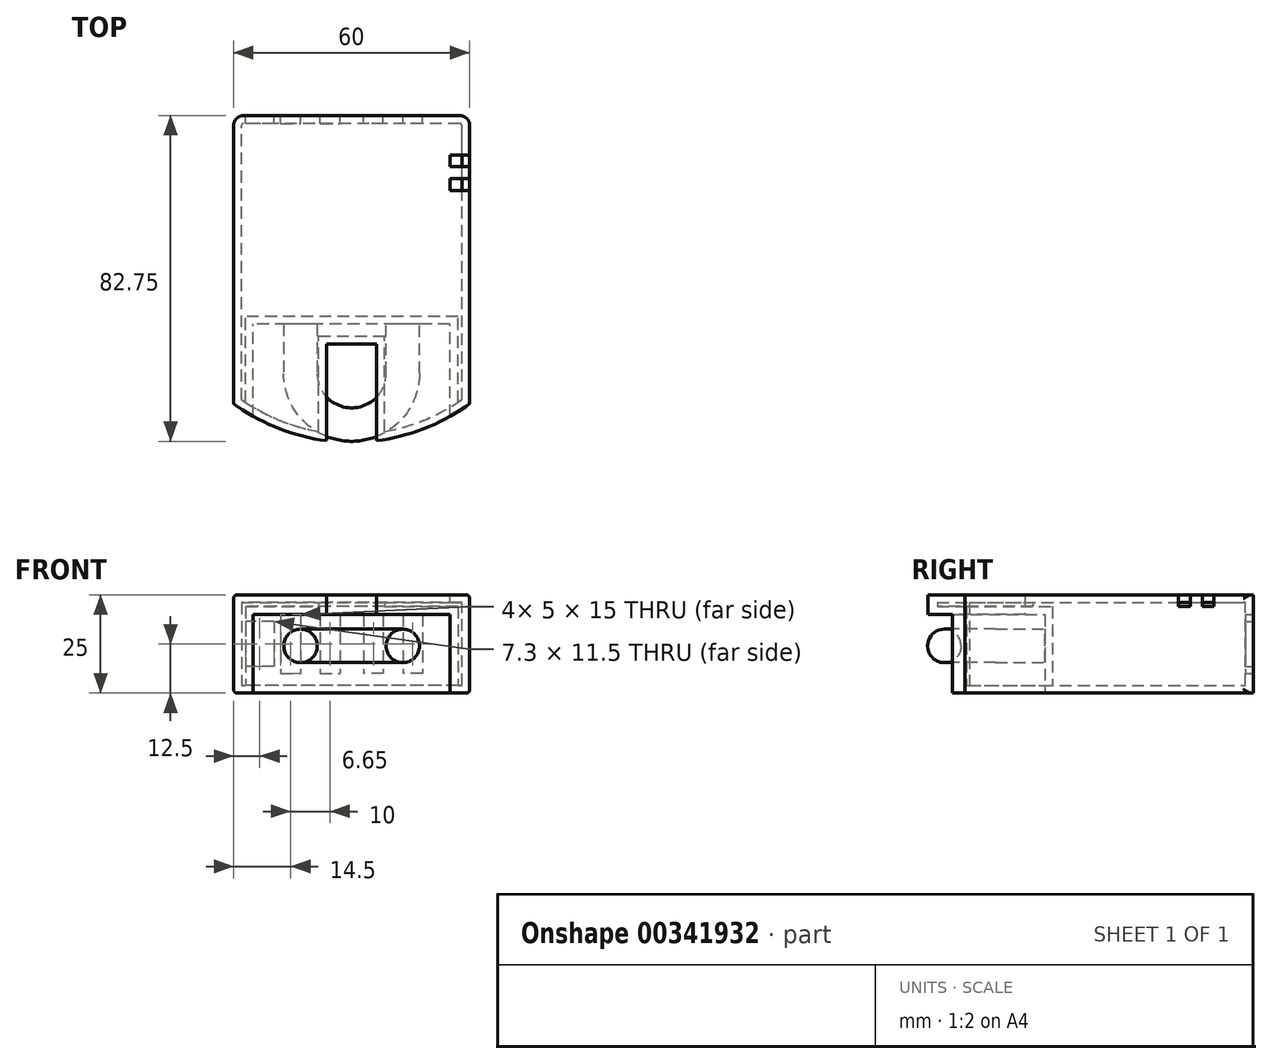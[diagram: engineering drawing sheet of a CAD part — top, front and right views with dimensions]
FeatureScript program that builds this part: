
annotation { "Feature Type Name" : "Feature", "Feature Type Description" : "" }
export const myFeature = defineFeature(function(context is Context, id is Id, definition is map)
    precondition{}
    {
        {
            var Q0;
            Q0=qCreatedBy(makeId("Top.planeOp"),FACE);
            var sketch = newSketch(context, id + "F0", { "sketchPlane" : qUnion([Q0])});
            skLineSegment(sketch, "E0.top", {"start": v(30, 36.6) * mm, "end": v(-30, 36.6) * mm});
            skLineSegment(sketch, "E0.left", {"start": v(30, -36.6) * mm, "end": v(30, 36.6) * mm});
            skLineSegment(sketch, "E0.right", {"start": v(-30, -36.6) * mm, "end": v(-30, 36.6) * mm});
            skPoint(sketch, "E0.middle", {"position": v(0, 0) * mm});
            skArc(sketch, "E1", {"start": v(-30, -36.6) * mm, "mid": v(0, -46.4) * mm, "end": v(30, -36.6) * mm});
            skSolve(sketch);
        }
        {
            var Q0;
            Q0=makeQuery(id+"F0.imprint","IMPRINT",FACE,{"disambiguationData":[TD([[makeQuery(id+"F0.imprint","IMPRINT",EDGE,{"derivedFrom":sQuery(id+"F0.wireOp",EDGE,"E0.bottom")}),-1.0]])]});
            var Q1;
            Q1=makeQuery(id+"F0.imprint","IMPRINT",FACE,{"disambiguationData":[TD([[makeQuery(id+"F0.imprint","IMPRINT",EDGE,{"derivedFrom":sQuery(id+"F0.wireOp",EDGE,"E0.top")}),1.0]])]});
            extrude(context, id + "F1", {"entities" : qUnion([Q0, Q1]), "depth" : 25 * mm});
        }
        {
            var Q0;
            Q0=qCreatedBy(makeId("Top.planeOp"),FACE);
            var sketch = newSketch(context, id + "F2", { "sketchPlane" : qUnion([Q0])});
            skLineSegment(sketch, "E2.bottom", {"start": v(-6.35, -46.4) * mm, "end": v(6.35, -46.4) * mm});
            skLineSegment(sketch, "E2.top", {"start": v(-6.35, -21.4) * mm, "end": v(6.35, -21.4) * mm});
            skLineSegment(sketch, "E2.left", {"start": v(-6.35, -46.4) * mm, "end": v(-6.35, -21.4) * mm});
            skLineSegment(sketch, "E2.right", {"start": v(6.35, -46.4) * mm, "end": v(6.35, -21.4) * mm});
            skPoint(sketch, "E2.middle", {"position": v(0, -33.9) * mm});
            skSolve(sketch);
        }
        {
            var Q0;
            Q0=makeQuery(id+"F1.opExtrude","SWEPT_EDGE",EDGE,{"disambiguationData":[OSD([sQuery(id+"F0.wireOp",EDGE,"E0.top"),sQuery(id+"F0.wireOp",EDGE,"E0.right")])]});
            var Q1;
            Q1=makeQuery(id+"F1.opExtrude","SWEPT_EDGE",EDGE,{"disambiguationData":[OSD([sQuery(id+"F0.wireOp",EDGE,"E0.top"),sQuery(id+"F0.wireOp",EDGE,"E0.left")])]});
            fillet(context, id + "F3", {"entities" : qUnion([Q0, Q1]), "radius" : 2.54 * mm, "tangentPropagation" : true, "allowEdgeOverflow" : false});
        }
        {
            var Q0;
            Q0=makeQuery(id+"F0.imprint","IMPRINT",FACE,{"disambiguationData":[TD([[makeQuery(id+"F0.imprint","IMPRINT",EDGE,{"derivedFrom":sQuery(id+"F0.wireOp",EDGE,"E0.top")}),1.0]])]});
            var sketch = newSketch(context, id + "F4", { "sketchPlane" : qUnion([Q0])});
            skLineSegment(sketch, "E3.bottom", {"start": v(25, -46.4) * mm, "end": v(-25, -46.4) * mm});
            skLineSegment(sketch, "E3.top", {"start": v(25, -16.4) * mm, "end": v(-25, -16.4) * mm});
            skLineSegment(sketch, "E3.left", {"start": v(25, -46.4) * mm, "end": v(25, -16.4) * mm});
            skLineSegment(sketch, "E3.right", {"start": v(-25, -46.4) * mm, "end": v(-25, -16.4) * mm});
            skPoint(sketch, "E3.middle", {"position": v(0, -31.4) * mm});
            skSolve(sketch);
        }
        {
            var Q0;
            Q0 = qSketchRegion(id + "F4", true);
            extrude(context, id + "F5", {"entities" : qUnion([Q0]), "operationType" : NewBodyOperationType.REMOVE, "depth" : 20 * mm});
        }
        {
            var Q0;
            Q0 = qSketchRegion(id + "F2", true);
            var Q1;
            Q1=makeQuery(id+"F1.opExtrude","CAP_FACE",FACE,{"disambiguationData":[OSD([sQuery(id+"F0.wireOp",EDGE,"E0.top"),sQuery(id+"F0.wireOp",EDGE,"E0.left"),sQuery(id+"F0.wireOp",EDGE,"E0.right"),sQuery(id+"F0.wireOp",EDGE,"E1")])],"isStart":false});
            extrude(context, id + "F6", {"entities" : qUnion([Q0]), "operationType" : NewBodyOperationType.REMOVE, "endBound" : BoundingType.UP_TO_SURFACE, "endBoundEntityFace" : qUnion([Q1]), "depth" : 25.4 * mm});
        }
        {
            var Q0;
            Q0=makeQuery(id+"F1.opExtrude","CAP_FACE",FACE,{"disambiguationData":[OSD([sQuery(id+"F0.wireOp",EDGE,"E0.top"),sQuery(id+"F0.wireOp",EDGE,"E0.left"),sQuery(id+"F0.wireOp",EDGE,"E0.right"),sQuery(id+"F0.wireOp",EDGE,"E1")])],"isStart":false});
            var Q1;
            Q1=makeQuery(id+"F1.opExtrude","SWEPT_BODY",BODY,{"disambiguationData":[OSD([sQuery(id+"F0.wireOp",EDGE,"E0.top"),sQuery(id+"F0.wireOp",EDGE,"E0.left"),sQuery(id+"F0.wireOp",EDGE,"E0.right"),sQuery(id+"F0.wireOp",EDGE,"E1")])]});
            shell(context, id + "F7", {"isHollow" : true, "entities" : qUnion([Q0]), "parts" : qUnion([Q1]), "thickness" : 2 * mm});
        }
        {
            var Q0;
            Q0=makeQuery(id+"F1.opExtrude","CAP_EDGE",EDGE,{"disambiguationData":[OSD([sQuery(id+"F0.wireOp",EDGE,"E0.left")])],"isStart":true});
            var Q1;
            Q1=makeQuery(id+"F1.opExtrude","CAP_EDGE",EDGE,{"disambiguationData":[OSD([sQuery(id+"F0.wireOp",EDGE,"E0.left")])],"isStart":false});
            var Q2;
            Q2=makeQuery(id+"F1.opExtrude","CAP_EDGE",EDGE,{"disambiguationData":[OSD([sQuery(id+"F0.wireOp",EDGE,"E0.right")])],"isStart":false});
            var Q3;
            Q3=makeQuery(id+"F1.opExtrude","CAP_EDGE",EDGE,{"disambiguationData":[OSD([sQuery(id+"F0.wireOp",EDGE,"E0.right")])],"isStart":true});
            fillet(context, id + "F8", {"entities" : qUnion([Q0, Q1, Q2, Q3]), "radius" : 1 * mm, "allowEdgeOverflow" : false});
        }
        {
            var Q0;
            Q0=makeQuery(id+"F5.boolean.opBoolean","COPY",FACE,{"derivedFrom":makeQuery(id+"F5.opExtrude","SWEPT_FACE",FACE,{"disambiguationData":[OSD([sQuery(id+"F4.wireOp",EDGE,"E3.top")])]})});
            var sketch = newSketch(context, id + "F9", { "sketchPlane" : qUnion([Q0])});
            skCircle(sketch, "E4", {"center": v(-13, 12) * mm, "radius": 5 * mm});
            skCircle(sketch, "E5.MirrorC", {"center": v(13, 12) * mm, "radius": 5 * mm});
            skSolve(sketch);
        }
        {
            var Q0;
            Q0=makeQuery(id+"F1.opExtrude","SWEPT_FACE",FACE,{"disambiguationData":[OSD([sQuery(id+"F0.wireOp",EDGE,"E0.top")])]});
            var sketch = newSketch(context, id + "F10", { "sketchPlane" : qUnion([Q0])});
            skLineSegment(sketch, "E6.bottom", {"start": v(-13, 5) * mm, "end": v(-18, 5) * mm});
            skLineSegment(sketch, "E6.top", {"start": v(-13, 20) * mm, "end": v(-18, 20) * mm});
            skLineSegment(sketch, "E6.left", {"start": v(-13, 5) * mm, "end": v(-13, 20) * mm});
            skLineSegment(sketch, "E6.right", {"start": v(-18, 5) * mm, "end": v(-18, 20) * mm});
            skPoint(sketch, "E6.middle", {"position": v(-15.5, 12.5) * mm});
            skLineSegment(sketch, "E7.MirrorCS", {"start": v(13, 5) * mm, "end": v(13, 20) * mm});
            skLineSegment(sketch, "E8.MirrorCS", {"start": v(13, 20) * mm, "end": v(18, 20) * mm});
            skLineSegment(sketch, "E9.MirrorCS", {"start": v(18, 5) * mm, "end": v(18, 20) * mm});
            skLineSegment(sketch, "E10.MirrorCS", {"start": v(13, 5) * mm, "end": v(18, 5) * mm});
            skLineSegment(sketch, "E11.bottom", {"start": v(-3, 5) * mm, "end": v(-8, 5) * mm});
            skLineSegment(sketch, "E11.top", {"start": v(-3, 20) * mm, "end": v(-8, 20) * mm});
            skLineSegment(sketch, "E11.left", {"start": v(-3, 5) * mm, "end": v(-3, 20) * mm});
            skLineSegment(sketch, "E11.right", {"start": v(-8, 5) * mm, "end": v(-8, 20) * mm});
            skPoint(sketch, "E11.middle", {"position": v(-5.5, 12.5) * mm});
            skLineSegment(sketch, "E12.MirrorCS", {"start": v(3, 20) * mm, "end": v(8, 20) * mm});
            skLineSegment(sketch, "E13.MirrorCS", {"start": v(8, 5) * mm, "end": v(8, 20) * mm});
            skLineSegment(sketch, "E14.MirrorCS", {"start": v(3, 5) * mm, "end": v(3, 20) * mm});
            skLineSegment(sketch, "E15.MirrorCS", {"start": v(3, 5) * mm, "end": v(8, 5) * mm});
            skSolve(sketch);
        }
        {
            var Q0;
            Q0 = qSketchRegion(id + "F10", true);
            extrude(context, id + "F11", {"entities" : qUnion([Q0]), "operationType" : NewBodyOperationType.REMOVE, "oppositeDirection" : true, "depth" : 10 * mm});
        }
        {
            var Q0;
            Q0=makeQuery(id+"F1.opExtrude","SWEPT_FACE",FACE,{"disambiguationData":[OSD([sQuery(id+"F0.wireOp",EDGE,"E0.top")])]});
            var sketch = newSketch(context, id + "F12", { "sketchPlane" : qUnion([Q0])});
            skLineSegment(sketch, "E16.bottom", {"start": v(27, 6.75) * mm, "end": v(19.7, 6.75) * mm});
            skLineSegment(sketch, "E16.top", {"start": v(27, 18.25) * mm, "end": v(19.7, 18.25) * mm});
            skLineSegment(sketch, "E16.left", {"start": v(27, 6.75) * mm, "end": v(27, 18.25) * mm});
            skLineSegment(sketch, "E16.right", {"start": v(19.7, 6.75) * mm, "end": v(19.7, 18.25) * mm});
            skPoint(sketch, "E16.middle", {"position": v(23.35, 12.5) * mm});
            skSolve(sketch);
        }
        {
            var Q0;
            Q0=makeQuery(id+"F12.imprint","IMPRINT",FACE,{"disambiguationData":[TD([[makeQuery(id+"F12.imprint","IMPRINT",EDGE,{"derivedFrom":sQuery(id+"F12.wireOp",EDGE,"E16.bottom")}),-1.0]])]});
            extrude(context, id + "F13", {"entities" : qUnion([Q0]), "operationType" : NewBodyOperationType.REMOVE, "oppositeDirection" : true, "depth" : 25.4 * mm});
        }
        {
            var Q0;
            Q0=qCreatedBy(makeId("Top.planeOp"),FACE);
            cPlane(context, id + "F14", {"entities" : qUnion([Q0]), "cplaneType" : CPlaneType.OFFSET, "offset" : 12 * mm, "width" : 152.4 * mm, "height" : 152.4 * mm});
        }
        {
            var Q0;
            Q0=qCreatedBy(id+"F14.planeOp",FACE);
            var sketch = newSketch(context, id + "F15", { "sketchPlane" : qUnion([Q0])});
            skLineSegment(sketch, "E17", {"start": v(-13, -16.4) * mm, "end": v(-13, -28.9) * mm});
            skLineSegment(sketch, "E18", {"start": v(13, -16.4) * mm, "end": v(13, -28.9) * mm});
            skArc(sketch, "E19", {"start": v(-13, -28.9) * mm, "mid": v(0, -41.9) * mm, "end": v(13, -28.9) * mm});
            skSolve(sketch);
        }
        {
            var Q0;
            Q0=makeQuery(id+"F9.imprint","IMPRINT",FACE,{"disambiguationData":[TD([[makeQuery(id+"F9.imprint","IMPRINT",EDGE,{"derivedFrom":sQuery(id+"F9.wireOp",EDGE,"E4")}),-1.0]])]});
            var sketch = newSketch(context, id + "F16", { "sketchPlane" : qUnion([Q0])});
            skCircle(sketch, "E20", {"center": v(-13, 12) * mm, "radius": 4.25 * mm});
            skSolve(sketch);
        }
        {
            var Q0;
            Q0 = qSketchRegion(id + "F16", true);
            var Q1;
            Q1=sQuery(id+"F15.wireOp",EDGE,"E17");
            var Q2;
            Q2=sQuery(id+"F15.wireOp",EDGE,"E19");
            var Q3;
            Q3=sQuery(id+"F15.wireOp",EDGE,"E18");
            sweep(context, id + "F17", {"operationType" : NewBodyOperationType.ADD, "profiles" : qUnion([Q0]), "path" : qUnion([Q1, Q2, Q3])});
        }
        {
            var Q0;
            Q0=makeQuery(id+"F1.opExtrude","CAP_FACE",FACE,{"disambiguationData":[OSD([sQuery(id+"F0.wireOp",EDGE,"E0.top"),sQuery(id+"F0.wireOp",EDGE,"E0.left"),sQuery(id+"F0.wireOp",EDGE,"E0.right"),sQuery(id+"F0.wireOp",EDGE,"E1")])],"isStart":false});
            var sketch = newSketch(context, id + "F18", { "sketchPlane" : qUnion([Q0])});
            skLineSegment(sketch, "E21.bottom", {"start": v(25, 26.6) * mm, "end": v(30, 26.6) * mm});
            skLineSegment(sketch, "E21.top", {"start": v(25, 23.6) * mm, "end": v(30, 23.6) * mm});
            skLineSegment(sketch, "E21.left", {"start": v(25, 26.6) * mm, "end": v(25, 23.6) * mm});
            skLineSegment(sketch, "E21.right", {"start": v(30, 26.6) * mm, "end": v(30, 23.6) * mm});
            skPoint(sketch, "E21.middle", {"position": v(27.5, 25.1) * mm});
            skLineSegment(sketch, "E22.bottom", {"start": v(25, 20.6) * mm, "end": v(30, 20.6) * mm});
            skLineSegment(sketch, "E22.top", {"start": v(25, 17.6) * mm, "end": v(30, 17.6) * mm});
            skLineSegment(sketch, "E22.left", {"start": v(25, 20.6) * mm, "end": v(25, 17.6) * mm});
            skLineSegment(sketch, "E22.right", {"start": v(30, 20.6) * mm, "end": v(30, 17.6) * mm});
            skPoint(sketch, "E22.middle", {"position": v(27.5, 19.1) * mm});
            skSolve(sketch);
        }
        {
            var Q0;
            Q0 = qSketchRegion(id + "F18", true);
            extrude(context, id + "F19", {"entities" : qUnion([Q0]), "operationType" : NewBodyOperationType.REMOVE, "oppositeDirection" : true, "depth" : 3 * mm});
        }
    });
